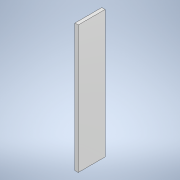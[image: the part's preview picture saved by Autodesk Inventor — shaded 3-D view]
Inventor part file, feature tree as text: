
AUTODESK INVENTOR PART (.ipt)
format: ipt  version: 2022 (Build 260153000, 153)  size: 103,424 bytes
history: native  units: mm
features: other x1, extrude x1, sketch x1
ambient origin geometry x8: Origin, YZ Plane, XZ Plane, XY Plane, X Axis, Y Axis, Z Axis, Center Point
bodies: Body1 (feature_tree)
feature tree (3):
  other  "ソリッド1"
  extrude  "押し出し1"  Depth=40.0mm
  sketch  "スケッチ1"
